# Revit family: Sanitary_Accessories_Sanindusa_New-Wc-Care-Folding-Supporting-Bar
name_source: partatom
category: Plumbing Fixtures
revit_build: Autodesk Revit 2018 (Build: 20170223_1515(x64)
units: mm (PartAtom-declared; Revit-internal decimal feet)

## family parameters
Always vertical = Yes
Cut with Voids When Loaded = No
OmniClass Number = 23.45.00.00
OmniClass Title = Sanitary, Laundry, and Cleaning Equipment
Part Type = Normal
Room Calculation Point = No
Round Connector Dimension = Use Diameter
Shared = No
Work Plane-Based = No

## types (1)
- Sanitary_Accessories_Sanindusa_New-Wc-Care-Folding-Supporting-Bar
    AssetType = Fixed
    BarCode = 5604815900491
    Color = Silver
    Constituents = Fixings not included
150 mm PVC flexible hose; ABS shower bracket, with adjustable height; Fixing Kit.
    Cost = 0 $
    Description = New wccare folding supporting bar 80
    Edition number = 1
    Element Type = GRAB BAR: Basic drop-down grab bar, for people with reduced mobility
    Features = Drop-down grab bar Ø 35mm, for PRM.
In the lowered position use as a grab bar, for standing up and assisting movement. For WCs or showers. Allows side access in the raised position.
Slowed down descent. Retained in upright position.
Stainless steel  for easy maintenance and hygiene.
    Finish = Brushed
    Installation Instructions = https://www.tec.sanindusa.pt
    InstallationDate = 1900-12-31T23:59:59
    Manufacturer = Sanindusa
    ManufacturerName = Sanindusa
    ManufacturerURL = www.tec.sanindusa.pt
    Material = Stainless steel
    ModelNumber = 4296413
    ModelReference = New Wccare
    Name = New wccare folding supporting bar
    NominalHeight = 220 mm  [stored 0.721785 ft]
    NominalLength = 800 mm  [stored 2.62467 ft]
    NominalWidth = 0 mm  [stored 0 ft]
    Pre-defined type (IFC) = FURNISHING ELEMENT
    Product Guid = d10925f8-61c9-4e1e-ac78-755861101868
    Product data url = https://bimobject.com
    ProductInformation = https://www.tec.sanindusa.pt
    ProductionYear = 2017
    Size = 80x22
    Type (IFC) = IfcFurnitureType
    URL = www.tec.sanindusa.pt
    Uniclass2015Version = Products v1.6
    Version = 2
    WarrantyDescription = https://www.tec.sanindusa.pt
The warranty will come into force from the moment the warranty detachable bulletin that accompanies the product is received at Sanindusa or from the moment the product is sold to the distributer
Only if the customer issues a writen and justified (Country laws, state laws, commercial strategy) request to Sanindusa, may the above mentioned warranties be the object of a possible change.
    WarrantyDurationParts = 5
    WarrantyDurationUnit = year
    WarrantyStartDate = 1900-12-31T23:59:59
1900-12-31T23:59:59
    Weight = 3.74 kg

note: [stored X ft] marks values corroborated as IEEE doubles in the binary element streams (Revit-internal decimal feet)

## geometry (parser evidence)
native form markers: Sweep x8
no freeform markers — native parametric forms only
